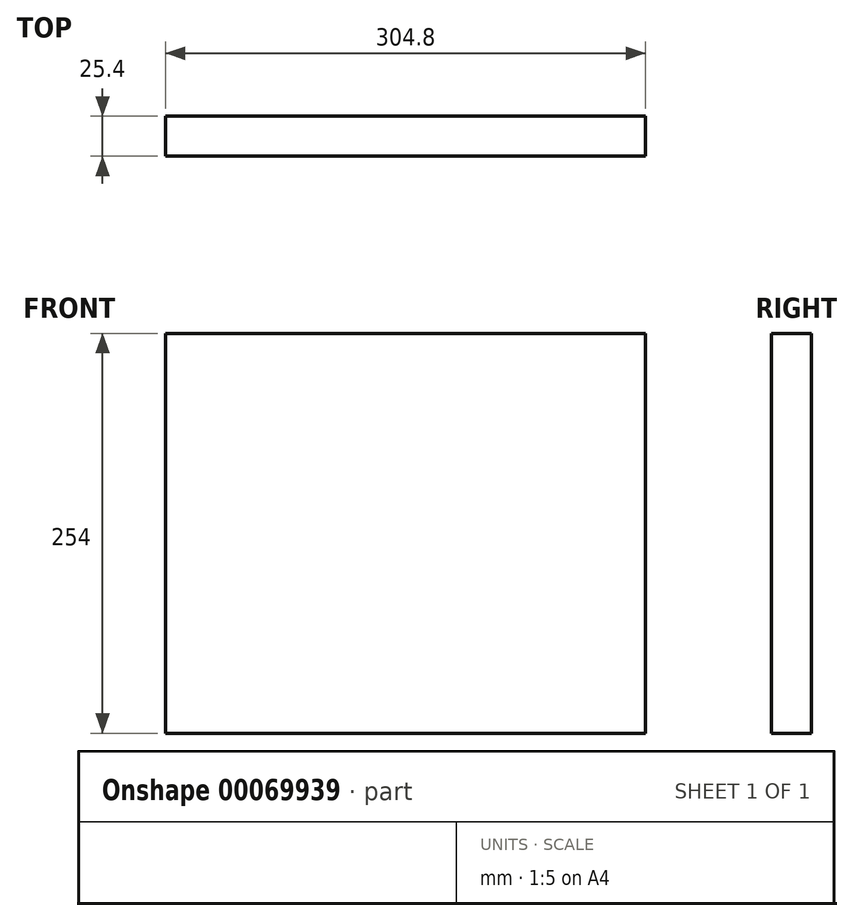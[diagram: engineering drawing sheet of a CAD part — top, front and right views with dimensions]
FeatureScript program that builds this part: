
annotation { "Feature Type Name" : "Feature", "Feature Type Description" : "" }
export const myFeature = defineFeature(function(context is Context, id is Id, definition is map)
    precondition{}
    {
        {
            var Q0;
            Q0=qCreatedBy(makeId("Front.planeOp"),FACE);
            var sketch = newSketch(context, id + "F0", { "sketchPlane" : qUnion([Q0])});
            skLineSegment(sketch, "E0.rect.bottom", {"start": v(152.4, -127) * mm, "end": v(-152.4, -127) * mm});
            skLineSegment(sketch, "E0.rect.top", {"start": v(152.4, 127) * mm, "end": v(-152.4, 127) * mm});
            skLineSegment(sketch, "E0.rect.left", {"start": v(152.4, -127) * mm, "end": v(152.4, 127) * mm});
            skLineSegment(sketch, "E0.rect.right", {"start": v(-152.4, -127) * mm, "end": v(-152.4, 127) * mm});
            skPoint(sketch, "E0.rect.middle", {"position": v(0, 0) * mm});
            skSolve(sketch);
        }
        {
            var Q0;
            Q0 = qSketchRegion(id + "F0", true);
            extrude(context, id + "F1", {"entities" : qUnion([Q0]), "depth" : 25.4 * mm});
        }
    });
